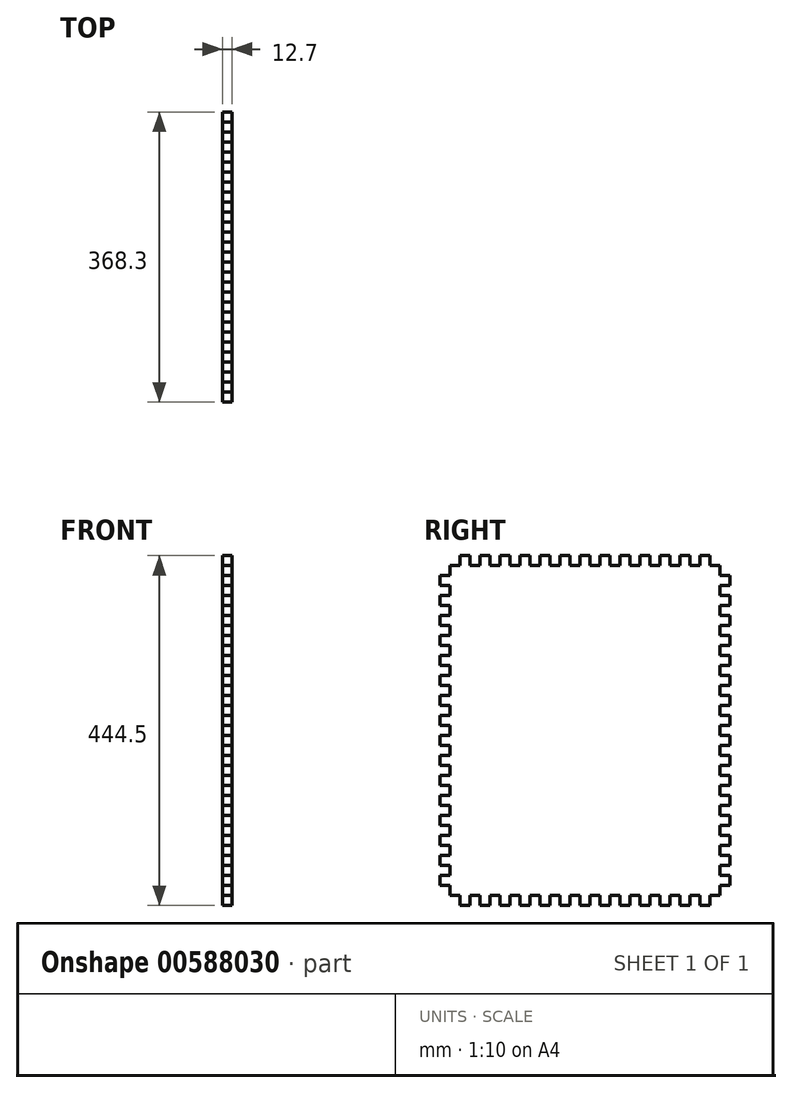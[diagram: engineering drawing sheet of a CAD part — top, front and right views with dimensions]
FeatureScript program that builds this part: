
annotation { "Feature Type Name" : "Feature", "Feature Type Description" : "" }
export const myFeature = defineFeature(function(context is Context, id is Id, definition is map)
    precondition{}
    {
        {
            var Q0;
            Q0=qCreatedBy(makeId("Right.planeOp"),FACE);
            var sketch = newSketch(context, id + "F0", { "sketchPlane" : qUnion([Q0])});
            skLineSegment(sketch, "E0", {"start": v(12.7, 12.87) * mm, "end": v(12.7, 25.57) * mm});
            skLineSegment(sketch, "E1", {"start": v(12.7, 25.57) * mm, "end": v(0, 25.57) * mm});
            skLineSegment(sketch, "E2.0.1.0", {"start": v(0, 25.57) * mm, "end": v(0, 38.27) * mm});
            skLineSegment(sketch, "E2.0.1.1", {"start": v(0, 38.27) * mm, "end": v(12.7, 38.27) * mm});
            skLineSegment(sketch, "E2.0.1.2", {"start": v(12.7, 38.27) * mm, "end": v(12.7, 50.97) * mm});
            skLineSegment(sketch, "E2.0.1.3", {"start": v(12.7, 50.97) * mm, "end": v(0, 50.97) * mm});
            skLineSegment(sketch, "E2.0.2.0", {"start": v(0, 50.97) * mm, "end": v(0, 63.67) * mm});
            skLineSegment(sketch, "E2.0.2.1", {"start": v(0, 63.67) * mm, "end": v(12.7, 63.67) * mm});
            skLineSegment(sketch, "E2.0.2.2", {"start": v(12.7, 63.67) * mm, "end": v(12.7, 76.37) * mm});
            skLineSegment(sketch, "E2.0.2.3", {"start": v(12.7, 76.37) * mm, "end": v(0, 76.37) * mm});
            skLineSegment(sketch, "E2.0.3.0", {"start": v(0, 76.37) * mm, "end": v(0, 89.07) * mm});
            skLineSegment(sketch, "E2.0.3.1", {"start": v(0, 89.07) * mm, "end": v(12.7, 89.07) * mm});
            skLineSegment(sketch, "E2.0.3.2", {"start": v(12.7, 89.07) * mm, "end": v(12.7, 101.77) * mm});
            skLineSegment(sketch, "E2.0.3.3", {"start": v(12.7, 101.77) * mm, "end": v(0, 101.77) * mm});
            skLineSegment(sketch, "E2.0.4.0", {"start": v(0, 101.77) * mm, "end": v(0, 114.47) * mm});
            skLineSegment(sketch, "E2.0.4.1", {"start": v(0, 114.47) * mm, "end": v(12.7, 114.47) * mm});
            skLineSegment(sketch, "E2.0.4.2", {"start": v(12.7, 114.47) * mm, "end": v(12.7, 127.17) * mm});
            skLineSegment(sketch, "E2.0.4.3", {"start": v(12.7, 127.17) * mm, "end": v(0, 127.17) * mm});
            skLineSegment(sketch, "E2.0.5.0", {"start": v(0, 127.17) * mm, "end": v(0, 139.87) * mm});
            skLineSegment(sketch, "E2.0.5.1", {"start": v(0, 139.87) * mm, "end": v(12.7, 139.87) * mm});
            skLineSegment(sketch, "E2.0.5.2", {"start": v(12.7, 139.87) * mm, "end": v(12.7, 152.57) * mm});
            skLineSegment(sketch, "E2.0.5.3", {"start": v(12.7, 152.57) * mm, "end": v(0, 152.57) * mm});
            skLineSegment(sketch, "E2.0.6.0", {"start": v(0, 152.57) * mm, "end": v(0, 165.27) * mm});
            skLineSegment(sketch, "E2.0.6.1", {"start": v(0, 165.27) * mm, "end": v(12.7, 165.27) * mm});
            skLineSegment(sketch, "E2.0.6.2", {"start": v(12.7, 165.27) * mm, "end": v(12.7, 177.97) * mm});
            skLineSegment(sketch, "E2.0.6.3", {"start": v(12.7, 177.97) * mm, "end": v(0, 177.97) * mm});
            skLineSegment(sketch, "E2.0.7.0", {"start": v(0, 177.97) * mm, "end": v(0, 190.67) * mm});
            skLineSegment(sketch, "E2.0.7.1", {"start": v(0, 190.67) * mm, "end": v(12.7, 190.67) * mm});
            skLineSegment(sketch, "E2.0.7.2", {"start": v(12.7, 190.67) * mm, "end": v(12.7, 203.37) * mm});
            skLineSegment(sketch, "E2.0.7.3", {"start": v(12.7, 203.37) * mm, "end": v(0, 203.37) * mm});
            skLineSegment(sketch, "E2.0.8.0", {"start": v(0, 203.37) * mm, "end": v(0, 216.07) * mm});
            skLineSegment(sketch, "E2.0.8.1", {"start": v(0, 216.07) * mm, "end": v(12.7, 216.07) * mm});
            skLineSegment(sketch, "E2.0.8.2", {"start": v(12.7, 216.07) * mm, "end": v(12.7, 228.77) * mm});
            skLineSegment(sketch, "E2.0.8.3", {"start": v(12.7, 228.77) * mm, "end": v(0, 228.77) * mm});
            skLineSegment(sketch, "E2.0.9.0", {"start": v(0, 228.77) * mm, "end": v(0, 241.47) * mm});
            skLineSegment(sketch, "E2.0.9.1", {"start": v(0, 241.47) * mm, "end": v(12.7, 241.47) * mm});
            skLineSegment(sketch, "E2.0.9.2", {"start": v(12.7, 241.47) * mm, "end": v(12.7, 254.17) * mm});
            skLineSegment(sketch, "E2.0.9.3", {"start": v(12.7, 254.17) * mm, "end": v(0, 254.17) * mm});
            skLineSegment(sketch, "E2.0.10.0", {"start": v(0, 254.17) * mm, "end": v(0, 266.87) * mm});
            skLineSegment(sketch, "E2.0.10.1", {"start": v(0, 266.87) * mm, "end": v(12.7, 266.87) * mm});
            skLineSegment(sketch, "E2.0.10.2", {"start": v(12.7, 266.87) * mm, "end": v(12.7, 279.57) * mm});
            skLineSegment(sketch, "E2.0.10.3", {"start": v(12.7, 279.57) * mm, "end": v(0, 279.57) * mm});
            skLineSegment(sketch, "E2.0.11.0", {"start": v(0, 279.57) * mm, "end": v(0, 292.27) * mm});
            skLineSegment(sketch, "E2.0.11.1", {"start": v(0, 292.27) * mm, "end": v(12.7, 292.27) * mm});
            skLineSegment(sketch, "E2.0.11.2", {"start": v(12.7, 292.27) * mm, "end": v(12.7, 304.97) * mm});
            skLineSegment(sketch, "E2.0.11.3", {"start": v(12.7, 304.97) * mm, "end": v(0, 304.97) * mm});
            skLineSegment(sketch, "E2.0.12.0", {"start": v(0, 304.97) * mm, "end": v(0, 317.67) * mm});
            skLineSegment(sketch, "E2.0.12.1", {"start": v(0, 317.67) * mm, "end": v(12.7, 317.67) * mm});
            skLineSegment(sketch, "E2.0.12.2", {"start": v(12.7, 317.67) * mm, "end": v(12.7, 330.37) * mm});
            skLineSegment(sketch, "E2.0.12.3", {"start": v(12.7, 330.37) * mm, "end": v(0, 330.37) * mm});
            skLineSegment(sketch, "E2.0.13.0", {"start": v(0, 330.37) * mm, "end": v(0, 343.07) * mm});
            skLineSegment(sketch, "E2.0.13.1", {"start": v(0, 343.07) * mm, "end": v(12.7, 343.07) * mm});
            skLineSegment(sketch, "E2.0.13.2", {"start": v(12.7, 343.07) * mm, "end": v(12.7, 355.77) * mm});
            skLineSegment(sketch, "E2.0.13.3", {"start": v(12.7, 355.77) * mm, "end": v(0, 355.77) * mm});
            skLineSegment(sketch, "E2.0.14.0", {"start": v(0, 355.77) * mm, "end": v(0, 368.47) * mm});
            skLineSegment(sketch, "E2.0.14.1", {"start": v(0, 368.47) * mm, "end": v(12.7, 368.47) * mm});
            skLineSegment(sketch, "E2.0.14.2", {"start": v(12.7, 368.47) * mm, "end": v(12.7, 381.17) * mm});
            skLineSegment(sketch, "E2.0.14.3", {"start": v(12.7, 381.17) * mm, "end": v(0, 381.17) * mm});
            skLineSegment(sketch, "E2.0.15.0", {"start": v(0, 381.17) * mm, "end": v(0, 393.87) * mm});
            skLineSegment(sketch, "E2.0.15.1", {"start": v(0, 393.87) * mm, "end": v(12.7, 393.87) * mm});
            skLineSegment(sketch, "E2.0.15.2", {"start": v(12.7, 393.87) * mm, "end": v(12.7, 406.57) * mm});
            skLineSegment(sketch, "E2.0.15.3", {"start": v(12.7, 406.57) * mm, "end": v(0, 406.57) * mm});
            skLineSegment(sketch, "E2.0.16.0", {"start": v(0, 406.57) * mm, "end": v(0, 419.27) * mm});
            skLineSegment(sketch, "E2.0.16.1", {"start": v(0, 419.27) * mm, "end": v(12.7, 419.27) * mm});
            skLineSegment(sketch, "E2.0.16.2", {"start": v(12.7, 419.27) * mm, "end": v(12.7, 431.97) * mm});
            skLineSegment(sketch, "E3", {"start": v(25.4, 431.97) * mm, "end": v(25.4, 444.67) * mm});
            skLineSegment(sketch, "E4.1.0.0", {"start": v(50.8, 431.97) * mm, "end": v(50.8, 444.67) * mm});
            skLineSegment(sketch, "E4.1.0.1", {"start": v(50.8, 444.67) * mm, "end": v(63.5, 444.67) * mm});
            skLineSegment(sketch, "E4.1.0.2", {"start": v(63.5, 444.67) * mm, "end": v(63.5, 431.97) * mm});
            skLineSegment(sketch, "E4.1.0.3", {"start": v(63.5, 431.97) * mm, "end": v(76.2, 431.97) * mm});
            skLineSegment(sketch, "E4.2.0.0", {"start": v(76.2, 431.97) * mm, "end": v(76.2, 444.67) * mm});
            skLineSegment(sketch, "E4.2.0.1", {"start": v(76.2, 444.67) * mm, "end": v(88.9, 444.67) * mm});
            skLineSegment(sketch, "E4.2.0.2", {"start": v(88.9, 444.67) * mm, "end": v(88.9, 431.97) * mm});
            skLineSegment(sketch, "E4.2.0.3", {"start": v(88.9, 431.97) * mm, "end": v(101.6, 431.97) * mm});
            skLineSegment(sketch, "E4.3.0.0", {"start": v(101.6, 431.97) * mm, "end": v(101.6, 444.67) * mm});
            skLineSegment(sketch, "E4.3.0.1", {"start": v(101.6, 444.67) * mm, "end": v(114.3, 444.67) * mm});
            skLineSegment(sketch, "E4.3.0.2", {"start": v(114.3, 444.67) * mm, "end": v(114.3, 431.97) * mm});
            skLineSegment(sketch, "E4.3.0.3", {"start": v(114.3, 431.97) * mm, "end": v(127, 431.97) * mm});
            skLineSegment(sketch, "E4.4.0.0", {"start": v(127, 431.97) * mm, "end": v(127, 444.67) * mm});
            skLineSegment(sketch, "E4.4.0.1", {"start": v(127, 444.67) * mm, "end": v(139.7, 444.67) * mm});
            skLineSegment(sketch, "E4.4.0.2", {"start": v(139.7, 444.67) * mm, "end": v(139.7, 431.97) * mm});
            skLineSegment(sketch, "E4.4.0.3", {"start": v(139.7, 431.97) * mm, "end": v(152.4, 431.97) * mm});
            skLineSegment(sketch, "E4.5.0.0", {"start": v(152.4, 431.97) * mm, "end": v(152.4, 444.67) * mm});
            skLineSegment(sketch, "E4.5.0.1", {"start": v(152.4, 444.67) * mm, "end": v(165.1, 444.67) * mm});
            skLineSegment(sketch, "E4.5.0.2", {"start": v(165.1, 444.67) * mm, "end": v(165.1, 431.97) * mm});
            skLineSegment(sketch, "E4.5.0.3", {"start": v(165.1, 431.97) * mm, "end": v(177.8, 431.97) * mm});
            skLineSegment(sketch, "E4.6.0.0", {"start": v(177.8, 431.97) * mm, "end": v(177.8, 444.67) * mm});
            skLineSegment(sketch, "E4.6.0.1", {"start": v(177.8, 444.67) * mm, "end": v(190.5, 444.67) * mm});
            skLineSegment(sketch, "E4.6.0.2", {"start": v(190.5, 444.67) * mm, "end": v(190.5, 431.97) * mm});
            skLineSegment(sketch, "E4.6.0.3", {"start": v(190.5, 431.97) * mm, "end": v(203.2, 431.97) * mm});
            skLineSegment(sketch, "E4.7.0.0", {"start": v(203.2, 431.97) * mm, "end": v(203.2, 444.67) * mm});
            skLineSegment(sketch, "E4.7.0.1", {"start": v(203.2, 444.67) * mm, "end": v(215.9, 444.67) * mm});
            skLineSegment(sketch, "E4.7.0.2", {"start": v(215.9, 444.67) * mm, "end": v(215.9, 431.97) * mm});
            skLineSegment(sketch, "E4.7.0.3", {"start": v(215.9, 431.97) * mm, "end": v(228.6, 431.97) * mm});
            skLineSegment(sketch, "E4.8.0.0", {"start": v(228.6, 431.97) * mm, "end": v(228.6, 444.67) * mm});
            skLineSegment(sketch, "E4.8.0.1", {"start": v(228.6, 444.67) * mm, "end": v(241.3, 444.67) * mm});
            skLineSegment(sketch, "E4.8.0.2", {"start": v(241.3, 444.67) * mm, "end": v(241.3, 431.97) * mm});
            skLineSegment(sketch, "E4.8.0.3", {"start": v(241.3, 431.97) * mm, "end": v(254, 431.97) * mm});
            skLineSegment(sketch, "E4.9.0.0", {"start": v(254, 431.97) * mm, "end": v(254, 444.67) * mm});
            skLineSegment(sketch, "E4.9.0.1", {"start": v(254, 444.67) * mm, "end": v(266.7, 444.67) * mm});
            skLineSegment(sketch, "E4.9.0.2", {"start": v(266.7, 444.67) * mm, "end": v(266.7, 431.97) * mm});
            skLineSegment(sketch, "E4.9.0.3", {"start": v(266.7, 431.97) * mm, "end": v(279.4, 431.97) * mm});
            skLineSegment(sketch, "E4.10.0.0", {"start": v(279.4, 431.97) * mm, "end": v(279.4, 444.67) * mm});
            skLineSegment(sketch, "E4.10.0.1", {"start": v(279.4, 444.67) * mm, "end": v(292.1, 444.67) * mm});
            skLineSegment(sketch, "E4.10.0.2", {"start": v(292.1, 444.67) * mm, "end": v(292.1, 431.97) * mm});
            skLineSegment(sketch, "E4.10.0.3", {"start": v(292.1, 431.97) * mm, "end": v(304.8, 431.97) * mm});
            skLineSegment(sketch, "E4.11.0.0", {"start": v(304.8, 431.97) * mm, "end": v(304.8, 444.67) * mm});
            skLineSegment(sketch, "E4.11.0.1", {"start": v(304.8, 444.67) * mm, "end": v(317.5, 444.67) * mm});
            skLineSegment(sketch, "E4.11.0.2", {"start": v(317.5, 444.67) * mm, "end": v(317.5, 431.97) * mm});
            skLineSegment(sketch, "E4.11.0.3", {"start": v(317.5, 431.97) * mm, "end": v(330.2, 431.97) * mm});
            skLineSegment(sketch, "E4.12.0.0", {"start": v(330.2, 431.97) * mm, "end": v(330.2, 444.67) * mm});
            skLineSegment(sketch, "E4.12.0.1", {"start": v(330.2, 444.67) * mm, "end": v(342.9, 444.67) * mm});
            skLineSegment(sketch, "E4.12.0.2", {"start": v(342.9, 444.67) * mm, "end": v(342.9, 431.97) * mm});
            skLineSegment(sketch, "E4.12.0.3", {"start": v(342.9, 431.97) * mm, "end": v(355.6, 431.97) * mm});
            skLineSegment(sketch, "E5", {"start": v(12.7, 431.97) * mm, "end": v(25.4, 431.97) * mm});
            skLineSegment(sketch, "E6", {"start": v(50.8, 431.97) * mm, "end": v(38.1, 431.97) * mm});
            skLineSegment(sketch, "E7", {"start": v(25.4, 444.67) * mm, "end": v(38.1, 444.67) * mm});
            skLineSegment(sketch, "E8", {"start": v(38.1, 444.67) * mm, "end": v(38.1, 431.97) * mm});
            skPoint(sketch, "E9.endSnap0", {"position": v(184.15, 222.42) * mm});
            skLineSegment(sketch, "E10.MirrorCS", {"start": v(368.3, 419.27) * mm, "end": v(355.6, 419.27) * mm});
            skLineSegment(sketch, "E11.MirrorCS", {"start": v(368.3, 216.07) * mm, "end": v(355.6, 216.07) * mm});
            skLineSegment(sketch, "E12.MirrorCS", {"start": v(368.3, 266.87) * mm, "end": v(355.6, 266.87) * mm});
            skLineSegment(sketch, "E13.MirrorCS", {"start": v(355.6, 89.07) * mm, "end": v(355.6, 101.77) * mm});
            skLineSegment(sketch, "E14.MirrorCS", {"start": v(368.3, 76.37) * mm, "end": v(368.3, 89.07) * mm});
            skLineSegment(sketch, "E15.MirrorCS", {"start": v(355.6, 127.17) * mm, "end": v(368.3, 127.17) * mm});
            skLineSegment(sketch, "E16.MirrorCS", {"start": v(368.3, 89.07) * mm, "end": v(355.6, 89.07) * mm});
            skLineSegment(sketch, "E17.MirrorCS", {"start": v(355.6, 228.77) * mm, "end": v(368.3, 228.77) * mm});
            skLineSegment(sketch, "E18.MirrorCS", {"start": v(355.6, 279.57) * mm, "end": v(368.3, 279.57) * mm});
            skLineSegment(sketch, "E19.MirrorCS", {"start": v(355.6, 63.67) * mm, "end": v(355.6, 76.37) * mm});
            skLineSegment(sketch, "E20.MirrorCS", {"start": v(355.6, 76.37) * mm, "end": v(368.3, 76.37) * mm});
            skLineSegment(sketch, "E21.MirrorCS", {"start": v(355.6, 241.47) * mm, "end": v(355.6, 254.17) * mm});
            skLineSegment(sketch, "E22.MirrorCS", {"start": v(355.6, 406.57) * mm, "end": v(368.3, 406.57) * mm});
            skLineSegment(sketch, "E23.MirrorCS", {"start": v(368.3, 127.17) * mm, "end": v(368.3, 139.87) * mm});
            skLineSegment(sketch, "E24.MirrorCS", {"start": v(355.6, 190.67) * mm, "end": v(355.6, 203.37) * mm});
            skLineSegment(sketch, "E25.MirrorCS", {"start": v(355.6, 152.57) * mm, "end": v(368.3, 152.57) * mm});
            skLineSegment(sketch, "E26.MirrorCS", {"start": v(355.6, 304.97) * mm, "end": v(368.3, 304.97) * mm});
            skLineSegment(sketch, "E27.MirrorCS", {"start": v(355.6, 139.87) * mm, "end": v(355.6, 152.57) * mm});
            skLineSegment(sketch, "E28.MirrorCS", {"start": v(355.6, 292.27) * mm, "end": v(355.6, 304.97) * mm});
            skLineSegment(sketch, "E29.MirrorCS", {"start": v(355.6, 419.27) * mm, "end": v(355.6, 431.97) * mm});
            skLineSegment(sketch, "E30.MirrorCS", {"start": v(368.3, 139.87) * mm, "end": v(355.6, 139.87) * mm});
            skLineSegment(sketch, "E31.MirrorCS", {"start": v(368.3, 317.67) * mm, "end": v(355.6, 317.67) * mm});
            skLineSegment(sketch, "E32.MirrorCS", {"start": v(355.6, 101.77) * mm, "end": v(368.3, 101.77) * mm});
            skLineSegment(sketch, "E33.MirrorCS", {"start": v(368.3, 368.47) * mm, "end": v(355.6, 368.47) * mm});
            skLineSegment(sketch, "E34.MirrorCS", {"start": v(368.3, 165.27) * mm, "end": v(355.6, 165.27) * mm});
            skLineSegment(sketch, "E35.MirrorCS", {"start": v(355.6, 114.47) * mm, "end": v(355.6, 127.17) * mm});
            skLineSegment(sketch, "E36.MirrorCS", {"start": v(355.6, 368.47) * mm, "end": v(355.6, 381.17) * mm});
            skLineSegment(sketch, "E37.MirrorCS", {"start": v(355.6, 266.87) * mm, "end": v(355.6, 279.57) * mm});
            skLineSegment(sketch, "E38.MirrorCS", {"start": v(355.6, 165.27) * mm, "end": v(355.6, 177.97) * mm});
            skLineSegment(sketch, "E39.MirrorCS", {"start": v(368.3, 152.57) * mm, "end": v(368.3, 165.27) * mm});
            skLineSegment(sketch, "E40.MirrorCS", {"start": v(355.6, 330.37) * mm, "end": v(368.3, 330.37) * mm});
            skLineSegment(sketch, "E41.MirrorCS", {"start": v(355.6, 381.17) * mm, "end": v(368.3, 381.17) * mm});
            skLineSegment(sketch, "E42.MirrorCS", {"start": v(368.3, 279.57) * mm, "end": v(368.3, 292.27) * mm});
            skLineSegment(sketch, "E43.MirrorCS", {"start": v(368.3, 330.37) * mm, "end": v(368.3, 343.07) * mm});
            skLineSegment(sketch, "E44.MirrorCS", {"start": v(368.3, 343.07) * mm, "end": v(355.6, 343.07) * mm});
            skLineSegment(sketch, "E45.MirrorCS", {"start": v(368.3, 381.17) * mm, "end": v(368.3, 393.87) * mm});
            skLineSegment(sketch, "E46.MirrorCS", {"start": v(355.6, 343.07) * mm, "end": v(355.6, 355.77) * mm});
            skLineSegment(sketch, "E47.MirrorCS", {"start": v(355.6, 177.97) * mm, "end": v(368.3, 177.97) * mm});
            skLineSegment(sketch, "E48.MirrorCS", {"start": v(355.6, 254.17) * mm, "end": v(368.3, 254.17) * mm});
            skLineSegment(sketch, "E49.MirrorCS", {"start": v(368.3, 304.97) * mm, "end": v(368.3, 317.67) * mm});
            skLineSegment(sketch, "E50.MirrorCS", {"start": v(368.3, 177.97) * mm, "end": v(368.3, 190.67) * mm});
            skLineSegment(sketch, "E51.MirrorCS", {"start": v(355.6, 317.67) * mm, "end": v(355.6, 330.37) * mm});
            skLineSegment(sketch, "E52.MirrorCS", {"start": v(368.3, 406.57) * mm, "end": v(368.3, 419.27) * mm});
            skLineSegment(sketch, "E53.MirrorCS", {"start": v(355.6, 203.37) * mm, "end": v(368.3, 203.37) * mm});
            skLineSegment(sketch, "E54.MirrorCS", {"start": v(368.3, 393.87) * mm, "end": v(355.6, 393.87) * mm});
            skLineSegment(sketch, "E55.MirrorCS", {"start": v(355.6, 393.87) * mm, "end": v(355.6, 406.57) * mm});
            skLineSegment(sketch, "E56.MirrorCS", {"start": v(355.6, 216.07) * mm, "end": v(355.6, 228.77) * mm});
            skLineSegment(sketch, "E57.MirrorCS", {"start": v(355.6, 355.77) * mm, "end": v(368.3, 355.77) * mm});
            skLineSegment(sketch, "E58.MirrorCS", {"start": v(368.3, 241.47) * mm, "end": v(355.6, 241.47) * mm});
            skLineSegment(sketch, "E59.MirrorCS", {"start": v(368.3, 190.67) * mm, "end": v(355.6, 190.67) * mm});
            skLineSegment(sketch, "E60.MirrorCS", {"start": v(368.3, 254.17) * mm, "end": v(368.3, 266.87) * mm});
            skLineSegment(sketch, "E61.MirrorCS", {"start": v(368.3, 101.77) * mm, "end": v(368.3, 114.47) * mm});
            skLineSegment(sketch, "E62.MirrorCS", {"start": v(355.6, 12.87) * mm, "end": v(355.6, 25.57) * mm});
            skLineSegment(sketch, "E63.MirrorCS", {"start": v(368.3, 228.77) * mm, "end": v(368.3, 241.47) * mm});
            skLineSegment(sketch, "E64.MirrorCS", {"start": v(368.3, 63.67) * mm, "end": v(355.6, 63.67) * mm});
            skLineSegment(sketch, "E65.MirrorCS", {"start": v(355.6, 50.97) * mm, "end": v(368.3, 50.97) * mm});
            skLineSegment(sketch, "E66.MirrorCS", {"start": v(355.6, 38.27) * mm, "end": v(355.6, 50.97) * mm});
            skLineSegment(sketch, "E67.MirrorCS", {"start": v(368.3, 38.27) * mm, "end": v(355.6, 38.27) * mm});
            skLineSegment(sketch, "E68.MirrorCS", {"start": v(368.3, 292.27) * mm, "end": v(355.6, 292.27) * mm});
            skLineSegment(sketch, "E69.MirrorCS", {"start": v(368.3, 50.97) * mm, "end": v(368.3, 63.67) * mm});
            skLineSegment(sketch, "E70.MirrorCS", {"start": v(368.3, 203.37) * mm, "end": v(368.3, 216.07) * mm});
            skLineSegment(sketch, "E71.MirrorCS", {"start": v(368.3, 25.57) * mm, "end": v(368.3, 38.27) * mm});
            skLineSegment(sketch, "E72.MirrorCS", {"start": v(368.3, 114.47) * mm, "end": v(355.6, 114.47) * mm});
            skLineSegment(sketch, "E73.MirrorCS", {"start": v(368.3, 355.77) * mm, "end": v(368.3, 368.47) * mm});
            skLineSegment(sketch, "E74.MirrorCS", {"start": v(355.6, 25.57) * mm, "end": v(368.3, 25.57) * mm});
            skLineSegment(sketch, "E75.MirrorCS", {"start": v(127, 12.87) * mm, "end": v(127, 0.17) * mm});
            skLineSegment(sketch, "E76.MirrorCS", {"start": v(266.7, 0.17) * mm, "end": v(266.7, 12.87) * mm});
            skLineSegment(sketch, "E77.MirrorCS", {"start": v(304.8, 0.17) * mm, "end": v(317.5, 0.17) * mm});
            skLineSegment(sketch, "E78.MirrorCS", {"start": v(342.9, 0.17) * mm, "end": v(342.9, 12.87) * mm});
            skLineSegment(sketch, "E79.MirrorCS", {"start": v(241.3, 0.17) * mm, "end": v(241.3, 12.87) * mm});
            skLineSegment(sketch, "E80.MirrorCS", {"start": v(12.7, 12.87) * mm, "end": v(25.4, 12.87) * mm});
            skLineSegment(sketch, "E81.MirrorCS", {"start": v(101.6, 0.17) * mm, "end": v(114.3, 0.17) * mm});
            skLineSegment(sketch, "E82.MirrorCS", {"start": v(203.2, 0.17) * mm, "end": v(215.9, 0.17) * mm});
            skLineSegment(sketch, "E83.MirrorCS", {"start": v(139.7, 0.17) * mm, "end": v(139.7, 12.87) * mm});
            skLineSegment(sketch, "E84.MirrorCS", {"start": v(25.4, 0.17) * mm, "end": v(38.1, 0.17) * mm});
            skLineSegment(sketch, "E85.MirrorCS", {"start": v(50.8, 0.17) * mm, "end": v(63.5, 0.17) * mm});
            skLineSegment(sketch, "E86.MirrorCS", {"start": v(152.4, 0.17) * mm, "end": v(165.1, 0.17) * mm});
            skLineSegment(sketch, "E87.MirrorCS", {"start": v(203.2, 12.87) * mm, "end": v(203.2, 0.17) * mm});
            skLineSegment(sketch, "E88.MirrorCS", {"start": v(127, 0.17) * mm, "end": v(139.7, 0.17) * mm});
            skLineSegment(sketch, "E89.MirrorCS", {"start": v(177.8, 12.87) * mm, "end": v(177.8, 0.17) * mm});
            skLineSegment(sketch, "E90.MirrorCS", {"start": v(139.7, 12.87) * mm, "end": v(152.4, 12.87) * mm});
            skLineSegment(sketch, "E91.MirrorCS", {"start": v(304.8, 12.87) * mm, "end": v(304.8, 0.17) * mm});
            skLineSegment(sketch, "E92.MirrorCS", {"start": v(25.4, 12.87) * mm, "end": v(25.4, 0.17) * mm});
            skLineSegment(sketch, "E93.MirrorCS", {"start": v(76.2, 0.17) * mm, "end": v(88.9, 0.17) * mm});
            skLineSegment(sketch, "E94.MirrorCS", {"start": v(241.3, 12.87) * mm, "end": v(254, 12.87) * mm});
            skLineSegment(sketch, "E95.MirrorCS", {"start": v(114.3, 0.17) * mm, "end": v(114.3, 12.87) * mm});
            skLineSegment(sketch, "E96.MirrorCS", {"start": v(342.9, 12.87) * mm, "end": v(355.6, 12.87) * mm});
            skLineSegment(sketch, "E97.MirrorCS", {"start": v(63.5, 12.87) * mm, "end": v(76.2, 12.87) * mm});
            skLineSegment(sketch, "E98.MirrorCS", {"start": v(165.1, 12.87) * mm, "end": v(177.8, 12.87) * mm});
            skLineSegment(sketch, "E99.MirrorCS", {"start": v(190.5, 12.87) * mm, "end": v(203.2, 12.87) * mm});
            skLineSegment(sketch, "E100.MirrorCS", {"start": v(88.9, 12.87) * mm, "end": v(101.6, 12.87) * mm});
            skLineSegment(sketch, "E101.MirrorCS", {"start": v(266.7, 12.87) * mm, "end": v(279.4, 12.87) * mm});
            skLineSegment(sketch, "E102.MirrorCS", {"start": v(76.2, 12.87) * mm, "end": v(76.2, 0.17) * mm});
            skLineSegment(sketch, "E103.MirrorCS", {"start": v(38.1, 0.17) * mm, "end": v(38.1, 12.87) * mm});
            skLineSegment(sketch, "E104.MirrorCS", {"start": v(317.5, 12.87) * mm, "end": v(330.2, 12.87) * mm});
            skLineSegment(sketch, "E105.MirrorCS", {"start": v(101.6, 12.87) * mm, "end": v(101.6, 0.17) * mm});
            skLineSegment(sketch, "E106.MirrorCS", {"start": v(279.4, 12.87) * mm, "end": v(279.4, 0.17) * mm});
            skLineSegment(sketch, "E107.MirrorCS", {"start": v(50.8, 12.87) * mm, "end": v(38.1, 12.87) * mm});
            skLineSegment(sketch, "E108.MirrorCS", {"start": v(292.1, 0.17) * mm, "end": v(292.1, 12.87) * mm});
            skLineSegment(sketch, "E109.MirrorCS", {"start": v(254, 0.17) * mm, "end": v(266.7, 0.17) * mm});
            skLineSegment(sketch, "E110.MirrorCS", {"start": v(215.9, 12.87) * mm, "end": v(228.6, 12.87) * mm});
            skLineSegment(sketch, "E111.MirrorCS", {"start": v(330.2, 0.17) * mm, "end": v(342.9, 0.17) * mm});
            skLineSegment(sketch, "E112.MirrorCS", {"start": v(88.9, 0.17) * mm, "end": v(88.9, 12.87) * mm});
            skLineSegment(sketch, "E113.MirrorCS", {"start": v(190.5, 0.17) * mm, "end": v(190.5, 12.87) * mm});
            skLineSegment(sketch, "E114.MirrorCS", {"start": v(228.6, 0.17) * mm, "end": v(241.3, 0.17) * mm});
            skLineSegment(sketch, "E115.MirrorCS", {"start": v(152.4, 12.87) * mm, "end": v(152.4, 0.17) * mm});
            skLineSegment(sketch, "E116.MirrorCS", {"start": v(254, 12.87) * mm, "end": v(254, 0.17) * mm});
            skLineSegment(sketch, "E117.MirrorCS", {"start": v(50.8, 12.87) * mm, "end": v(50.8, 0.17) * mm});
            skLineSegment(sketch, "E118.MirrorCS", {"start": v(279.4, 0.17) * mm, "end": v(292.1, 0.17) * mm});
            skLineSegment(sketch, "E119.MirrorCS", {"start": v(177.8, 0.17) * mm, "end": v(190.5, 0.17) * mm});
            skLineSegment(sketch, "E120.MirrorCS", {"start": v(228.6, 12.87) * mm, "end": v(228.6, 0.17) * mm});
            skLineSegment(sketch, "E121.MirrorCS", {"start": v(63.5, 0.17) * mm, "end": v(63.5, 12.87) * mm});
            skLineSegment(sketch, "E122.MirrorCS", {"start": v(330.2, 12.87) * mm, "end": v(330.2, 0.17) * mm});
            skLineSegment(sketch, "E123.MirrorCS", {"start": v(114.3, 12.87) * mm, "end": v(127, 12.87) * mm});
            skLineSegment(sketch, "E124.MirrorCS", {"start": v(165.1, 0.17) * mm, "end": v(165.1, 12.87) * mm});
            skLineSegment(sketch, "E125.MirrorCS", {"start": v(292.1, 12.87) * mm, "end": v(304.8, 12.87) * mm});
            skLineSegment(sketch, "E126.MirrorCS", {"start": v(215.9, 0.17) * mm, "end": v(215.9, 12.87) * mm});
            skLineSegment(sketch, "E127.MirrorCS", {"start": v(317.5, 0.17) * mm, "end": v(317.5, 12.87) * mm});
            skSolve(sketch);
        }
        {
            var Q0;
            Q0=makeQuery(id+"F0.imprint","IMPRINT",FACE,{"disambiguationData":[TD([[makeQuery(id+"F0.imprint","IMPRINT",EDGE,{"derivedFrom":sQuery(id+"F0.wireOp",EDGE,"E0")}),-1.0]])]});
            extrude(context, id + "F1", {"entities" : qUnion([Q0]), "depth" : 12.7 * mm, "offsetDistance" : 25.4 * mm});
        }
    });
